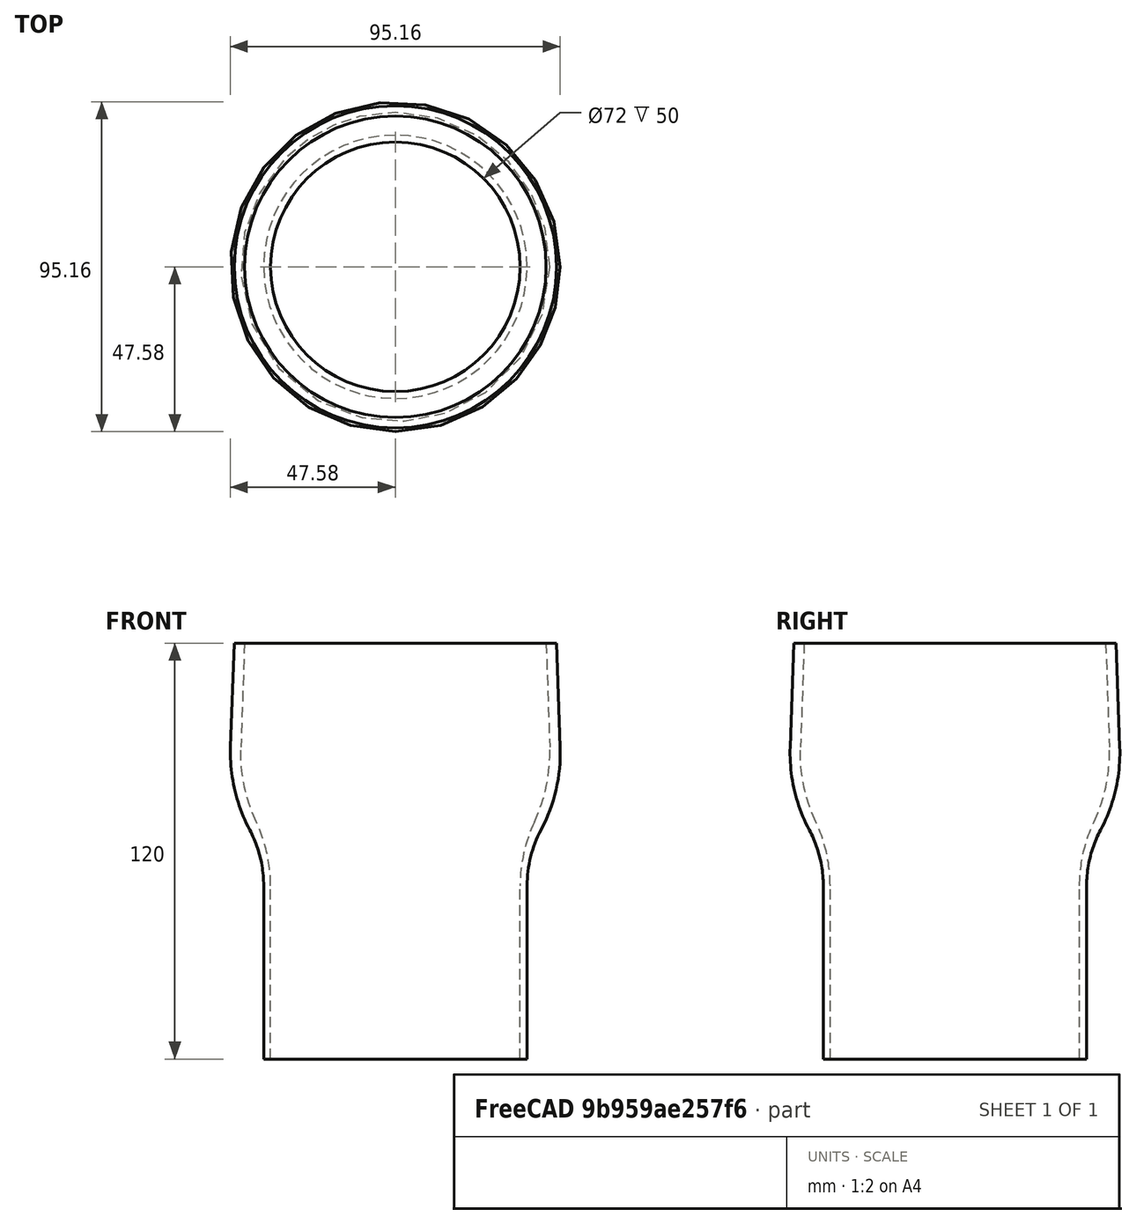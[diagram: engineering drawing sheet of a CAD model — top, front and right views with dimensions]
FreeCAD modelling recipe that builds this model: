
FCSTD DOCUMENT  (FreeCAD 0.19R)
Label: 4to3inchduct
License: All rights reserved
LicenseURL: http://en.wikipedia.org/wiki/All_rights_reserved
objects: Sketcher::SketchObject×1, PartDesign::Revolution×1, PartDesign::Body×1, Mesh::Feature×1
note: 4 computed .brp shape members not serialized (recipe doc carries the construction recipe); baked Part::Feature solids carry a one-line shape summary decoded from their .brp

FEATURE [Sketcher::SketchObject] Sketch
  FullyConstrained = true
  MapMode = 5
  Placement = pos=(0,0,0) rot=(1,0,0;1.5708rad)
  Support = -> [XZ_Plane]
  sketch-geometry (10):
    g0: LineSegment StartX=36 StartY=0 StartZ=0 EndX=36 EndY=50 EndZ=0
    g1: LineSegment StartX=36 StartY=0 StartZ=0 EndX=38 EndY=0 EndZ=0
    g2: LineSegment StartX=38 StartY=0 StartZ=0 EndX=38 EndY=50 EndZ=0
    g3: LineSegment StartX=43.4982 StartY=120 StartZ=0 EndX=44.5452 EndY=90.0183 EndZ=0
    g4: LineSegment StartX=46.5 StartY=120 StartZ=0 EndX=47.547 EndY=90.0183 EndZ=0
    g5: ArcOfCircle CenterX=79.2869 CenterY=50 CenterZ=0 NormalX=0 NormalY=0 NormalZ=1 AngleXU=0 Radius=43.2869 StartAngle=2.70204 EndAngle=3.14159
    g6: ArcOfCircle CenterX=-2.33492 CenterY=88.3812 CenterZ=0 NormalX=0 NormalY=0 NormalZ=1 AngleXU=0 Radius=46.9086 StartAngle=5.84363 EndAngle=6.31809
    g7: ArcOfCircle CenterX=72.3701 CenterY=50 CenterZ=0 NormalX=0 NormalY=0 NormalZ=1 AngleXU=0 Radius=34.3701 StartAngle=2.65243 EndAngle=3.14159
    g8: ArcOfCircle CenterX=0.291732 CenterY=88.3681 CenterZ=0 NormalX=0 NormalY=0 NormalZ=1 AngleXU=0 Radius=47.2841 StartAngle=5.79402 EndAngle=6.31809
    g9: LineSegment StartX=43.4982 StartY=120 StartZ=0 EndX=46.5 EndY=120 EndZ=0
  constraints (28):
    c: PointOnObject(g0,g-1)
    c: Vertical(g0)
    c: Coincident(g1,g0)
    c: PointOnObject(g1,g-1)
    c: Coincident(g2,g1)
    c: Vertical(g2)
    c: Parallel(g4,g3)
    c: Distance(g4,g3) = 3
    c: Angle(g4) = -1.53589
    c: Distance(g2,g0) = 2
    c: Tangent(g6,g5) = 1.5708
    c: Tangent(g5,g0) = 1.5708
    c: Tangent(g6,g3) = 1.5708
    c: Tangent(g8,g4) = 1.5708
    c: Tangent(g8,g7) = 1.5708
    c: Coincident(g9,g3)
    c: Coincident(g9,g4)
    c: Tangent(g7,g2) = 1.5708
    c: DistanceY(g3,g4) = 0
    c: DistanceY(g2,g0) = 0
    c: DistanceX(g1) = 38
    c: Distance(g2) = 50
    c: Distance(g3) = 30
    c: DistanceY(g3) = 120
    c: DistanceY(g7) = 66.15
    c: DistanceY(g5) = 68.42
    c: Horizontal(g9)
    c: DistanceX(g4) = 46.5
FEATURE [PartDesign::Revolution] Revolution
  Angle = 360
  Axis = (0,2e-16,1)
  Base = (0,0,0)
  Placement = pos=(0,0,0) rot=(1,0,0;1.5708rad)
  Profile = -> Sketch
  ReferenceAxis = -> Sketch [V_Axis]
  Reversed = true
FEATURE [PartDesign::Body] Body
  Group = -> [Sketch,Revolution]
  Origin = -> Origin
  Tip = -> Revolution
FEATURE [Mesh::Feature] Mesh  label="Revolution (Meshed)"
